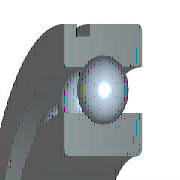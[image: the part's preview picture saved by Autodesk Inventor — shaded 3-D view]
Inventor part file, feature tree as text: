
AUTODESK INVENTOR PART (.ipt)
format: ipt  version: 2015 (Build 190159000, 159)  size: 358,400 bytes
history: native  units: mm (DEFAULTED — no unit token found)
features: sketch x1, other x1, pattern_circular x1
ambient origin geometry x8: Origin, YZ Plane, XZ Plane, XY Plane, X Axis, Y Axis, Z Axis, Center Point
bodies: Solid1 (feature_tree)
feature tree (3):
  sketch  "草图"  dims[d0=3.12mm d17=90.0deg d18=90.0deg d1=0.3mm d2=130.0mm d3=360.0deg d4=0.0mm d5=0.0mm d6=0.0mm d7=20.0mm d8=32.0mm d9=26.0mm d10=30.92mm d11=23.912mm d12=23.912mm d13=23.912mm d14=0.0mm d15=7.0mm d16=7.0mm d19=1.166667mm d20=2.333333mm d22=3.5mm d23=0.0mm d24=0.0mm]
  other  "轴承体"
  pattern_circular  "IDS_ARRAYBALL[SIMPL:T]"  Angle=90.0deg  [1 undecoded]
note: 1 required parameter value undecoded (feature->parameter linkage not recoverable at this tier; creation-order binding heuristic only, values carry confidence <= 0.55)
